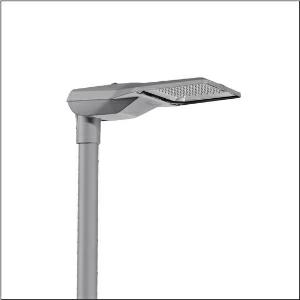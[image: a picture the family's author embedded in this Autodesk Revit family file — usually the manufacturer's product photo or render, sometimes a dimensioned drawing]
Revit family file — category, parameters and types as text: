
# Revit family: streetlight_sl_21_midi___st0_5a_5xe3b43s08lb_de93
name_source: partatom
category: Lighting Fixtures
units: mm (PartAtom-declared; Revit-internal decimal feet)

## family parameters
Cut with Voids When Loaded = No
Host = Face
Light Source = No
Part Type = Normal
Room Calculation Point = No
Round Connector Dimension = Use Diameter
Shared = No

## types (1)
- --- (1 x LED, 14950 lm, 98.3 W, 4000K)
    Apparent Load = 98 VA
    CIE Flux Codes = 41 75 97 100 100
    Color Rendering = 70
    Color Temperature = 4000K
    Default Elevation = 1800 mm
    Description = Streetlight SL 21 midi, mast luminaire, primary light control with lens, of PMMA, primary optical cover: cover, of toughened safety glass, transparent, light distribution: ST0.5a, light emission: direct distribution, primary light characteristic: asymmetric, installation type: side-entry, post-top, LED, High Power LED, rated luminous flux: 14.950lm, luminous efficacy: 152lm/W, light colour: 740, colour temperature: 4000K, control: overheat protection, constant luminous flux control, time-dependent luminous flux control, flexible luminous flux parameterisation, presetting dimming logarithmic, mains connection: 230..240V, AC, 50/60Hz, start of lifetime: 98W, end of service life: 101W, reduction: 45W, luminaire housing, of diecast aluminium, powder-coated, Siteco® metallic grey (DB 702S), corrosivity category C5 mid according to DIN EN ISO 12944, please order mast flange separately, inclination adjustable: 0°, 5°, 10°, 15°, sealing non-destructively replaceable, multi-level sealing system, length: 644mm, width: 335mm, height: 110mm, mast flange for spigot size: 42mm (side-entry): 5XC10008XM4, 60/48mm (side-entry/post-top): 5XC10108XM2, 76/60mm (side-entry/post-top): 5XC10108XM1, Smart Interface above, protection rating (complete): IP66, insulation class (complete): insulation class II (safety insulation), certification: CE, ENEC, ENEC+, VDE, impact resistance: IK09, permissible operating ambient temperature for outdoor applications: -40..+50°C, standard-compliant lighting for roads and squares, packaging unit: 1 piece

Light Distribution: ST0.5a
    Height = 111 mm
    Lamp = 1 x LED
    Lamp Light Flux = 14950 lm
    Lamp Power = 98.3 W
    Lamp count = 1
    Length = 644 mm
    Luminous efficacy = 152 lm/W
    Manufacturer = Siteco
    ModVariant = No
    Model = 5XE3B43S08LB
    Number of Poles = 1
    OnlyDefault = Yes
    Power Factor = 1
    Product Name = Streetlight SL 21 midi | ST0.5a
    Product group = mast luminaire | pylon top
    ProductGroupID = 6100
    Protection Class = Protection class II
    Protection Degree = IP 66
    RLX_Detail_Level = 1
    RLX_Emergency_Light_Flux = 0 lm
    RLX_Emergency_Type = 0
    RLX_Emergency_Type_DB = No
    RlxData = <blob elided: 101437 chars, md5=aebff418>
    Socket = socket
    Standby Power = 0 W
    System Light Flux = 14950 lm
    System Power = 98 W
    Type Comments = factory setting: luminous flux: 100 % | dim-lin: 254 | 1020 mA
    Type Image = l_1004302.jpg
    URL = http://relux.com
    VarID = @adj_144311
    Voltage = 0 V
    Weight = 0.00 kg
    Width = 336 mm

## geometry (parser evidence)
native form markers: Blend x4, Sweep x9
no freeform markers — native parametric forms only
